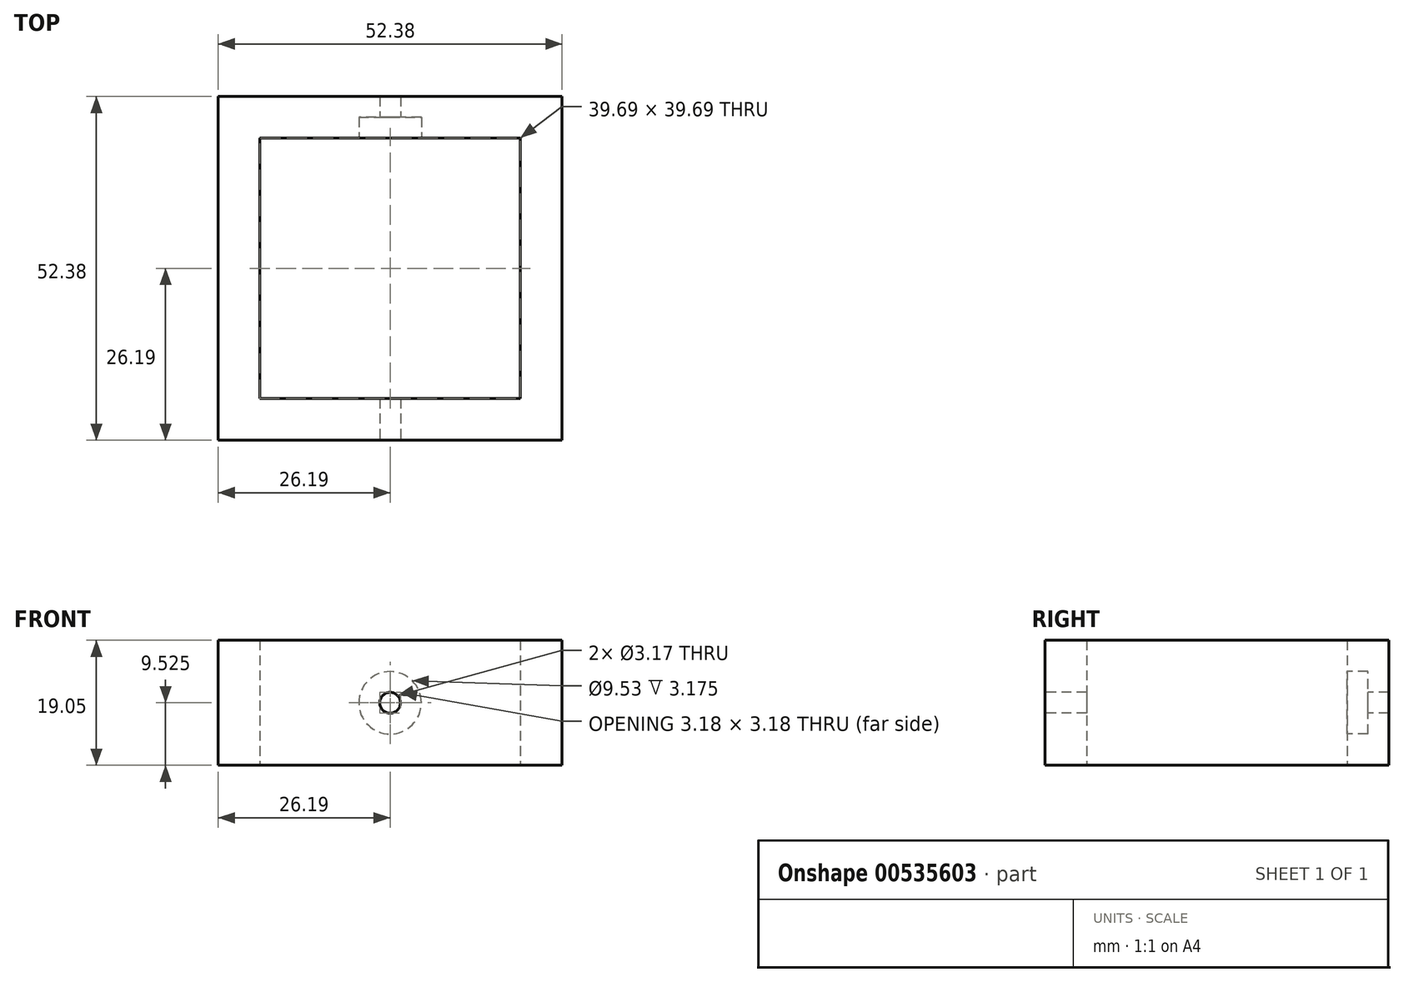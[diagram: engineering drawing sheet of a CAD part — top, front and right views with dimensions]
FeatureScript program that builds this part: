
annotation { "Feature Type Name" : "Feature", "Feature Type Description" : "" }
export const myFeature = defineFeature(function(context is Context, id is Id, definition is map)
    precondition{}
    {
        {
            var Q0;
            Q0=qCreatedBy(makeId("Top.planeOp"),FACE);
            var sketch = newSketch(context, id + "F0", { "sketchPlane" : qUnion([Q0])});
            skLineSegment(sketch, "E0.bottom", {"start": v(0, 0) * mm, "end": v(38.1, 0) * mm});
            skLineSegment(sketch, "E0.top", {"start": v(0, 38.1) * mm, "end": v(38.1, 38.1) * mm});
            skLineSegment(sketch, "E0.left", {"start": v(0, 0) * mm, "end": v(0, 38.1) * mm});
            skLineSegment(sketch, "E0.right", {"start": v(38.1, 0) * mm, "end": v(38.1, 38.1) * mm});
            skLineSegment(sketch, "E1.bottom", {"start": v(-0.8, 38.9) * mm, "end": v(38.9, 38.9) * mm});
            skLineSegment(sketch, "E1.top", {"start": v(-0.8, -0.8) * mm, "end": v(38.9, -0.8) * mm});
            skLineSegment(sketch, "E1.left", {"start": v(-0.8, 38.9) * mm, "end": v(-0.8, -0.8) * mm});
            skLineSegment(sketch, "E1.right", {"start": v(38.9, 38.9) * mm, "end": v(38.9, -0.8) * mm});
            skLineSegment(sketch, "E2.bottom", {"start": v(-7.14, 45.24) * mm, "end": v(45.24, 45.24) * mm});
            skLineSegment(sketch, "E2.top", {"start": v(-7.14, -7.14) * mm, "end": v(45.24, -7.14) * mm});
            skLineSegment(sketch, "E2.left", {"start": v(-7.14, 45.24) * mm, "end": v(-7.14, -7.14) * mm});
            skLineSegment(sketch, "E2.right", {"start": v(45.24, 45.24) * mm, "end": v(45.24, -7.14) * mm});
            skSolve(sketch);
        }
        {
            var Q0;
            Q0=makeQuery(id+"F0.imprint","IMPRINT",FACE,{"disambiguationData":[TD([[makeQuery(id+"F0.imprint","IMPRINT",EDGE,{"derivedFrom":sQuery(id+"F0.wireOp",EDGE,"E1.bottom")}),1.0]])]});
            extrude(context, id + "F1", {"entities" : qUnion([Q0]), "depth" : 19.05 * mm, "offsetDistance" : 25.4 * mm});
        }
        {
            var Q0;
            Q0=makeQuery(id+"F1.opExtrude","SWEPT_FACE",FACE,{"disambiguationData":[OSD([sQuery(id+"F0.wireOp",EDGE,"E1.bottom")])]});
            var sketch = newSketch(context, id + "F2", { "sketchPlane" : qUnion([Q0])});
            skCircle(sketch, "E3", {"center": v(19.05, 9.53) * mm, "radius": 1.59 * mm});
            skCircle(sketch, "E4", {"center": v(19.05, 9.53) * mm, "radius": 4.76 * mm});
            skSolve(sketch);
        }
        {
            var Q0;
            Q0=makeQuery(id+"F2.imprint","IMPRINT",FACE,{"disambiguationData":[TD([[makeQuery(id+"F2.imprint","IMPRINT",EDGE,{"derivedFrom":sQuery(id+"F2.wireOp",EDGE,"E3")}),1.0]])]});
            extrude(context, id + "F3", {"entities" : qUnion([Q0]), "operationType" : NewBodyOperationType.REMOVE, "oppositeDirection" : true, "depth" : 25.4 * mm, "offsetDistance" : 25.4 * mm});
        }
        {
            var Q0;
            Q0=makeQuery(id+"F2.imprint","IMPRINT",FACE,{"disambiguationData":[TD([[makeQuery(id+"F2.imprint","IMPRINT",EDGE,{"derivedFrom":sQuery(id+"F2.wireOp",EDGE,"E3")}),-1.0]])]});
            extrude(context, id + "F4", {"entities" : qUnion([Q0]), "operationType" : NewBodyOperationType.REMOVE, "oppositeDirection" : true, "depth" : 3.17 * mm, "offsetDistance" : 25.4 * mm});
        }
        {
            var Q0;
            Q0=makeQuery(id+"F1.opExtrude","SWEPT_FACE",FACE,{"disambiguationData":[OSD([sQuery(id+"F0.wireOp",EDGE,"E2.top")])]});
            var sketch = newSketch(context, id + "F5", { "sketchPlane" : qUnion([Q0])});
            skPoint(sketch, "E5", {"position": v(19.05, 19.05) * mm});
            skPoint(sketch, "E6", {"position": v(-7.14, 9.53) * mm});
            skPoint(sketch, "E7", {"position": v(19.05, 9.53) * mm});
            skSolve(sketch);
        }
        {
            var Q0;
            Q0=sQuery(id+"F5.wireOp",VERTEX,"E7");
            var Q1;
            Q1=makeQuery(id+"F1.opExtrude","SWEPT_BODY",BODY,{"disambiguationData":[OSD([sQuery(id+"F0.wireOp",EDGE,"E1.bottom"),sQuery(id+"F0.wireOp",EDGE,"E1.top"),sQuery(id+"F0.wireOp",EDGE,"E1.left"),sQuery(id+"F0.wireOp",EDGE,"E1.right"),sQuery(id+"F0.wireOp",EDGE,"E2.bottom"),sQuery(id+"F0.wireOp",EDGE,"E2.top"),sQuery(id+"F0.wireOp",EDGE,"E2.left"),sQuery(id+"F0.wireOp",EDGE,"E2.right")])]});
            hole(context, id + "F6", {"style" : HoleStyle.SIMPLE, "endStyle" : HoleEndStyle.THROUGH, "holeDiameter" : 3.17 * mm, "isTappedThrough" : true, "tappedDepth" : 12.7 * mm, "tapClearance" : 3, "locations" : qUnion([Q0]), "scope" : qUnion([Q1])});
        }
    });
